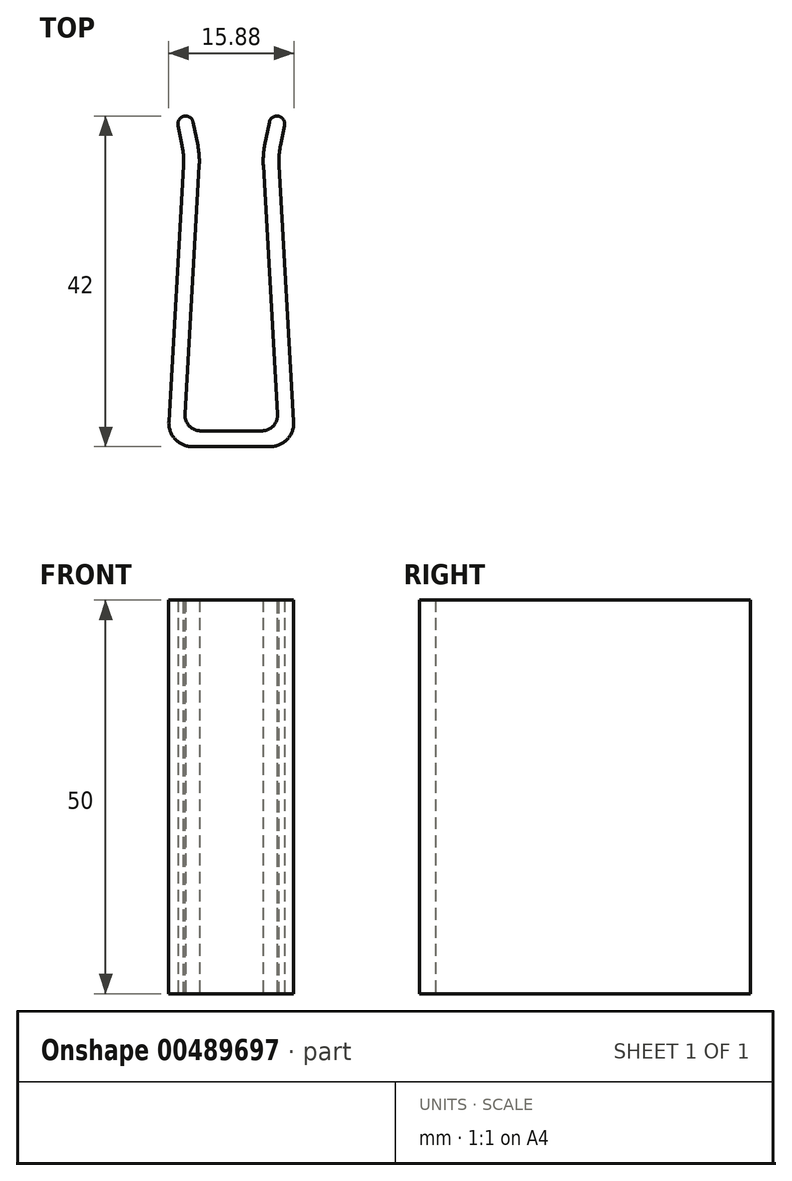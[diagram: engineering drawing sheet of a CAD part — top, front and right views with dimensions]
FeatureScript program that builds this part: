
annotation { "Feature Type Name" : "Feature", "Feature Type Description" : "" }
export const myFeature = defineFeature(function(context is Context, id is Id, definition is map)
    precondition{}
    {
        {
            var Q0;
            Q0=qCreatedBy(makeId("Top.planeOp"),FACE);
            var sketch = newSketch(context, id + "F0", { "sketchPlane" : qUnion([Q0])});
            skLineSegment(sketch, "E0", {"start": v(0, 0) * mm, "end": v(6, 0) * mm});
            skLineSegment(sketch, "E1", {"start": v(6, 0) * mm, "end": v(4, 35) * mm});
            skLineSegment(sketch, "E2", {"start": v(4, 35) * mm, "end": v(5, 40) * mm});
            skLineSegment(sketch, "E3", {"start": v(5, 40) * mm, "end": v(7, 40) * mm});
            skLineSegment(sketch, "E4", {"start": v(7, 40) * mm, "end": v(6, 35) * mm});
            skLineSegment(sketch, "E5", {"start": v(6, 35) * mm, "end": v(8.11, -2) * mm});
            skLineSegment(sketch, "E6", {"start": v(8.11, -2) * mm, "end": v(0, -2) * mm});
            skLineSegment(sketch, "E7", {"start": v(0, -2) * mm, "end": v(0, 0) * mm});
            skSolve(sketch);
        }
        {
            var Q0;
            Q0=makeQuery(id+"F0.imprint","IMPRINT",FACE,{"disambiguationData":[TD([[makeQuery(id+"F0.imprint","IMPRINT",EDGE,{"derivedFrom":sQuery(id+"F0.wireOp",EDGE,"E0")}),-1.0]])]});
            extrude(context, id + "F1", {"entities" : qUnion([Q0]), "depth" : 50 * mm});
        }
        {
            var Q0;
            Q0=makeQuery(id+"F1.opExtrude","SWEPT_BODY",BODY,{"disambiguationData":[OSD([sQuery(id+"F0.wireOp",EDGE,"E0"),sQuery(id+"F0.wireOp",EDGE,"E1"),sQuery(id+"F0.wireOp",EDGE,"E2"),sQuery(id+"F0.wireOp",EDGE,"E3"),sQuery(id+"F0.wireOp",EDGE,"E4"),sQuery(id+"F0.wireOp",EDGE,"E5"),sQuery(id+"F0.wireOp",EDGE,"E6"),sQuery(id+"F0.wireOp",EDGE,"E7")])]});
            var Q1;
            Q1=makeQuery(id+"F1.opExtrude","SWEPT_FACE",FACE,{"disambiguationData":[OSD([sQuery(id+"F0.wireOp",EDGE,"E7")])]});
            mirror(context, id + "F2", {"operationType" : NewBodyOperationType.ADD, "entities" : qUnion([Q0]), "mirrorPlane" : qUnion([Q1])});
        }
        {
            var Q0;
            Q0=makeQuery(id+"F1.opExtrude","SWEPT_EDGE",EDGE,{"disambiguationData":[OSD([sQuery(id+"F0.wireOp",EDGE,"E0"),sQuery(id+"F0.wireOp",EDGE,"E1")])]});
            fillet(context, id + "F3", {"entities" : qUnion([Q0]), "radius" : 2 * mm, "tangentPropagation" : true, "allowEdgeOverflow" : false});
        }
        {
            var Q0;
            Q0=makeQuery(id+"F1.opExtrude","SWEPT_EDGE",EDGE,{"disambiguationData":[OSD([sQuery(id+"F0.wireOp",EDGE,"E5"),sQuery(id+"F0.wireOp",EDGE,"E6")])]});
            fillet(context, id + "F4", {"entities" : qUnion([Q0]), "radius" : 3 * mm, "tangentPropagation" : true, "allowEdgeOverflow" : false});
        }
        {
            var Q0;
            Q0=makeQuery(id+"F2.opPattern","COPY",EDGE,{"derivedFrom":makeQuery(id+"F1.opExtrude","SWEPT_EDGE",EDGE,{"disambiguationData":[OSD([sQuery(id+"F0.wireOp",EDGE,"E0"),sQuery(id+"F0.wireOp",EDGE,"E1")])]}),"instanceName":"1"});
            fillet(context, id + "F5", {"entities" : qUnion([Q0]), "radius" : 2 * mm, "tangentPropagation" : true, "allowEdgeOverflow" : false});
        }
        {
            var Q0;
            Q0=makeQuery(id+"F2.opPattern","COPY",EDGE,{"derivedFrom":makeQuery(id+"F1.opExtrude","SWEPT_EDGE",EDGE,{"disambiguationData":[OSD([sQuery(id+"F0.wireOp",EDGE,"E5"),sQuery(id+"F0.wireOp",EDGE,"E6")])]}),"instanceName":"1"});
            fillet(context, id + "F6", {"entities" : qUnion([Q0]), "radius" : 3 * mm, "tangentPropagation" : true, "allowEdgeOverflow" : false});
        }
        {
            var Q0;
            Q0=makeQuery(id+"F2.opPattern","COPY",EDGE,{"derivedFrom":makeQuery(id+"F1.opExtrude","SWEPT_EDGE",EDGE,{"disambiguationData":[OSD([sQuery(id+"F0.wireOp",EDGE,"E2"),sQuery(id+"F0.wireOp",EDGE,"E3")])]}),"instanceName":"1"});
            var Q1;
            Q1=makeQuery(id+"F2.opPattern","COPY",EDGE,{"derivedFrom":makeQuery(id+"F1.opExtrude","SWEPT_EDGE",EDGE,{"disambiguationData":[OSD([sQuery(id+"F0.wireOp",EDGE,"E3"),sQuery(id+"F0.wireOp",EDGE,"E4")])]}),"instanceName":"1"});
            var Q2;
            Q2=makeQuery(id+"F1.opExtrude","SWEPT_EDGE",EDGE,{"disambiguationData":[OSD([sQuery(id+"F0.wireOp",EDGE,"E2"),sQuery(id+"F0.wireOp",EDGE,"E3")])]});
            var Q3;
            Q3=makeQuery(id+"F1.opExtrude","SWEPT_EDGE",EDGE,{"disambiguationData":[OSD([sQuery(id+"F0.wireOp",EDGE,"E3"),sQuery(id+"F0.wireOp",EDGE,"E4")])]});
            fillet(context, id + "F7", {"entities" : qUnion([Q0, Q1, Q2, Q3]), "radius" : 1 * mm, "tangentPropagation" : true, "allowEdgeOverflow" : false});
        }
        {
            var Q0;
            Q0=makeQuery(id+"F2.opPattern","COPY",EDGE,{"derivedFrom":makeQuery(id+"F1.opExtrude","SWEPT_EDGE",EDGE,{"disambiguationData":[OSD([sQuery(id+"F0.wireOp",EDGE,"E1"),sQuery(id+"F0.wireOp",EDGE,"E2")])]}),"instanceName":"1"});
            var Q1;
            Q1=makeQuery(id+"F1.opExtrude","SWEPT_EDGE",EDGE,{"disambiguationData":[OSD([sQuery(id+"F0.wireOp",EDGE,"E1"),sQuery(id+"F0.wireOp",EDGE,"E2")])]});
            var Q2;
            Q2=makeQuery(id+"F1.opExtrude","SWEPT_EDGE",EDGE,{"disambiguationData":[OSD([sQuery(id+"F0.wireOp",EDGE,"E4"),sQuery(id+"F0.wireOp",EDGE,"E5")])]});
            var Q3;
            Q3=makeQuery(id+"F2.opPattern","COPY",EDGE,{"derivedFrom":makeQuery(id+"F1.opExtrude","SWEPT_EDGE",EDGE,{"disambiguationData":[OSD([sQuery(id+"F0.wireOp",EDGE,"E4"),sQuery(id+"F0.wireOp",EDGE,"E5")])]}),"instanceName":"1"});
            fillet(context, id + "F8", {"entities" : qUnion([Q0, Q1, Q2, Q3]), "radius" : 10 * mm, "tangentPropagation" : true, "allowEdgeOverflow" : false});
        }
    });
